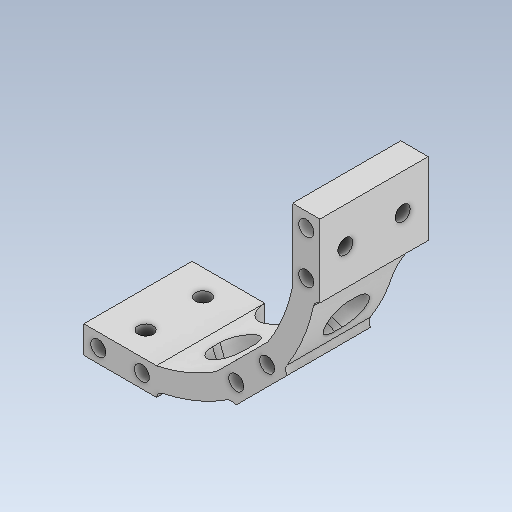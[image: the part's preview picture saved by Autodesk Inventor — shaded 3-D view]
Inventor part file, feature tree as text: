
AUTODESK INVENTOR PART (.ipt)
format: ipt  version: 2020 (Build 240168000, 168)  size: 504,320 bytes
history: native  units: mm
features: sketch x12, projected_geometry x10, extrude x8, reference x6, other x6, plane x4, hole x4, fillet x2, mirror x2, thicken_offset x2
ambient origin geometry x8: Origin, YZ Plane, XZ Plane, XY Plane, X Axis, Y Axis, Z Axis, Center Point
bodies: Solid1 (feature_tree)
feature tree (56):
  sketch  "Sketch1"  dims[d0=92.0mm d1=97.0mm]
  plane  "Work Plane1"
  extrude  "Extrusion1"  Depth=97.0mm
  extrude  "Extrusion2"  TaperAngle=60.0deg  [1 undecoded]
  extrude  "Extrusion3"  Depth=10.0mm TaperAngle=0.0deg
  extrude  "Extrusion4"  Depth=10.0mm TaperAngle=0.0deg
  extrude  "Extrusion5"  TaperAngle=45.0deg  [1 undecoded]
  extrude  "Extrusion6"  Depth=10.0mm
  hole  "Hole1"  [1 undecoded]
  sketch  "Sketch8"  dims[d18=4.0mm d19=4.0mm d20=4.0mm d21=4.0mm]
  plane  "Work Plane2"
  extrude  "Extrusion7"  Depth=4.0mm
  fillet  "Fillet1"  Radius=4.0mm
  fillet  "Fillet2"  Radius=4.0mm
  plane  "Work Plane3"
  hole  "Hole2"  [1 undecoded]
  mirror  "Mirror1"
  hole  "Hole3"  [1 undecoded]
  plane  "Work Plane4"
  extrude  "Extrusion8"  Depth=7.0mm TaperAngle=0.0deg
  mirror  "Mirror2"
  hole  "Hole4"  [1 undecoded]
  thicken_offset  "Thicken1"
  thicken_offset  "Thicken2"
  reference  "Reference1"
  reference  "Reference2"
  sketch  "Sketch2"  dims[d2=6.0mm d3=60.0deg]
  reference  "Reference3"
  projected_geometry  "Projected Loop1"
  sketch  "Sketch3"  dims[d4=60.0deg d5=10.0mm d6=0.0mm]
  reference  "Reference4"
  projected_geometry  "Projected Loop2"
  sketch  "Sketch4"  dims[d7=10.0mm d8=0.0mm d9=10.0mm d10=0.0mm]
  projected_geometry  "Projected Loop3"
  sketch  "Sketch5"  dims[d11=55.0mm d12=45.0deg]
  reference  "Reference5"
  projected_geometry  "Projected Loop4"
  sketch  "Sketch6"  dims[d13=10.0mm d14=10.0mm]
  projected_geometry  "Projected Loop5"
  reference  "Reference6"
  sketch  "Sketch7"  dims[d15=10.0mm d16=0.0mm d17=4.0mm]
  projected_geometry  "Projected Loop6"
  sketch  "Sketch9"  dims[d22=4.0mm d23=4.0mm]
  projected_geometry  "Projected Loop7"
  sketch  "Sketch10"  dims[d24=4.0mm d25=7.0mm d26=0.0mm]
  projected_geometry  "Projected Loop8"
  sketch  "Sketch11"  dims[d27=7.0mm d28=0.0mm]
  projected_geometry  "Projected Loop9"
  sketch  "Sketch12"  dims[d29=4.15mm d30=6.0mm d31=4.0mm d32=2.0mm d33=90.0deg d34=7.0mm d35=0.0mm d36=20.0mm d37=0.0mm d38=2.0mm d39=7.0mm d40=7.0mm d41=7.0mm d42=4.15mm d43=6.0mm d44=4.0mm d45=2.0mm d46=90.0deg d47=8.0mm d48=0.0mm d49=5.0mm d50=5.0mm d51=4.15mm d52=6.0mm d53=4.0mm d54=2.0mm d55=90.0deg d56=8.0mm d57=0.0mm d58=1.0mm d59=8.0mm d60=20.0mm d61=0.0mm d62=4.0mm d63=4.0mm d64=4.15mm d65=6.0mm d66=4.0mm d67=2.0mm d68=90.0deg d69=7.0mm d70=0.0mm d71=1.0mm d72=1.0mm d73=1.0mm d74=1.0mm]
  projected_geometry  "Projected Loop10"
  parser-record x1  (decoder bookkeeping rows leaked as tree rows — omitted from the tree; the rows remain in map.json)
  other  "reducer_1.iam"
  other  "xl_20:1"
  other  "motor_holder_1:1"
  other  "90_motor:1"
  other  "90motor_top:1"
note: 6 required parameter values undecoded (feature->parameter linkage not recoverable at this tier; creation-order binding heuristic only, values carry confidence <= 0.55)
note: 1 file-system path scrubbed to <path> (originals preserved in map.json)
